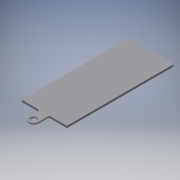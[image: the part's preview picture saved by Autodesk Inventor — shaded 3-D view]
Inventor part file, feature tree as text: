
AUTODESK INVENTOR PART (.ipt)
format: ipt  version: 2019 (Build 230136000, 136)  size: 191,488 bytes
history: native  units: mm
features: sketch x7, extrude x6, fillet x2, projected_geometry x2, hole x1
ambient origin geometry x8: Origin, YZ Plane, XZ Plane, XY Plane, X Axis, Y Axis, Z Axis, Center Point
bodies: Solid1 (feature_tree)
feature tree (18):
  extrude  "Extrusion1"  Depth=40.0mm
  extrude  "Extrusion2"  TaperAngle=0.0deg  [1 undecoded]
  extrude  "Extrusion4"  Depth=2.0mm
  hole  "Hole1"  [1 undecoded]
  extrude  "Extrusion6"  Depth=2.0mm
  fillet  "Fillet1"  [1 undecoded]
  fillet  "Fillet2"  [1 undecoded]
  extrude  "Extrusion7"  TaperAngle=0.0deg  [1 undecoded]
  extrude  "Extrusion8"  Depth=1.0mm
  sketch  "Sketch1"  dims[d1=100.0mm d2=40.0mm]
  sketch  "Sketch2"  dims[d3=4.0mm d4=0.0mm]
  projected_geometry  "Projected Loop1"
  sketch  "Sketch4"  dims[d5=2.0mm d6=2.0mm]
  sketch  "Sketch5"  dims[d7=0.0mm d12=10.0mm]
  sketch  "Sketch8"  dims[d13=10.0mm d14=2.0mm d15=0.0mm]
  sketch  "Sketch9"  dims[d16=5.5mm d17=6.0mm d18=9.4mm d19=2.0mm d20=90.0deg d21=8.0mm d22=20.594885mm d27=45.0deg]
  sketch  "Sketch10"  dims[d28=2.0mm d29=0.0mm d30=1.0mm d31=1.0mm d32=4.0mm d33=5.0mm d34=2.0mm d35=0.0mm d36=2.0mm d37=0.0mm]
  projected_geometry  "Projected Loop4"
note: 5 required parameter values undecoded (feature->parameter linkage not recoverable at this tier; creation-order binding heuristic only, values carry confidence <= 0.55)
